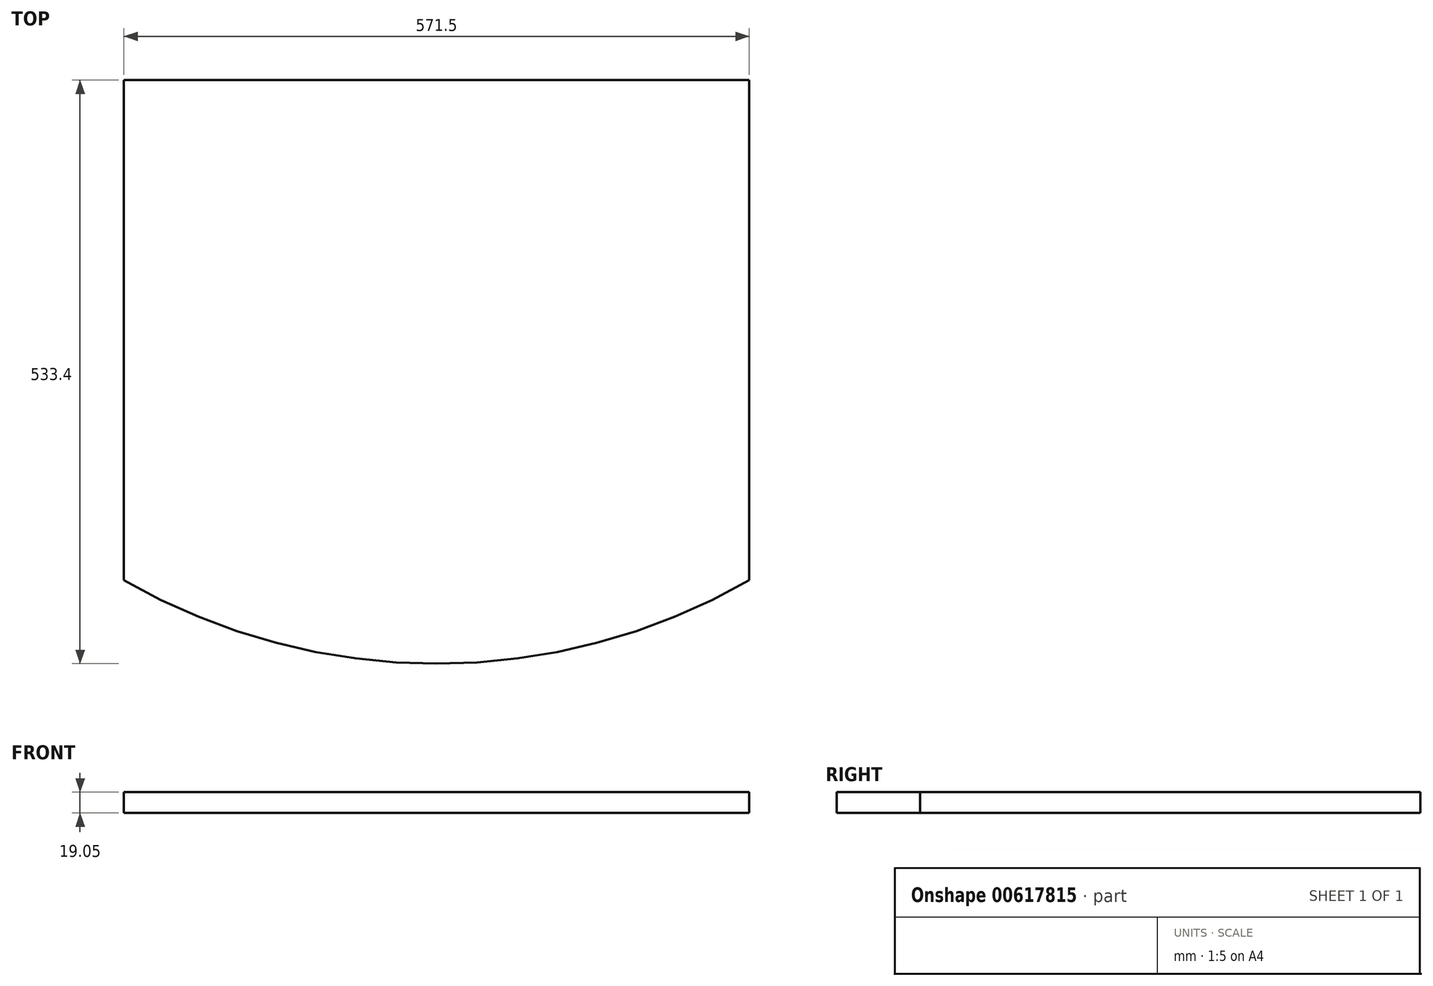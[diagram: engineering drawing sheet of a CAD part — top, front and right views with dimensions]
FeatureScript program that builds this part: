
annotation { "Feature Type Name" : "Feature", "Feature Type Description" : "" }
export const myFeature = defineFeature(function(context is Context, id is Id, definition is map)
    precondition{}
    {
        {
            var Q0;
            Q0=qCreatedBy(makeId("Top.planeOp"),FACE);
            var sketch = newSketch(context, id + "F0", { "sketchPlane" : qUnion([Q0])});
            skLineSegment(sketch, "E0.bottom", {"start": v(-285.75, 228.6) * mm, "end": v(285.75, 228.6) * mm});
            skLineSegment(sketch, "E0.top", {"start": v(-285.75, -228.6) * mm, "end": v(285.75, -228.6) * mm});
            skLineSegment(sketch, "E0.left", {"start": v(-285.75, 228.6) * mm, "end": v(-285.75, -228.6) * mm});
            skLineSegment(sketch, "E0.right", {"start": v(285.75, 228.6) * mm, "end": v(285.75, -228.6) * mm});
            skPoint(sketch, "E0.middle", {"position": v(0, 0) * mm});
            skLineSegment(sketch, "E1", {"start": v(0, -228.6) * mm, "end": v(0, -304.8) * mm});
            skPoint(sketch, "E1.endSnap0", {"position": v(0, -228.6) * mm});
            skArc(sketch, "E2", {"start": v(-285.75, -228.6) * mm, "mid": v(0, -304.8) * mm, "end": v(285.75, -228.6) * mm});
            skSolve(sketch);
        }
        {
            var Q0;
            Q0=makeQuery(id+"F0.imprint","IMPRINT",FACE,{"disambiguationData":[TD([[makeQuery(id+"F0.imprint","IMPRINT",EDGE,{"derivedFrom":sQuery(id+"F0.wireOp",EDGE,"E0.bottom")}),-1.0]])]});
            var Q1;
            {var subQ3=sQuery(id+"F0.wireOp",EDGE,"E1");Q1=makeQuery(id+"F0.imprint","IMPRINT",FACE,{"disambiguationData":[TD([[makeQuery(id+"F0.imprint","IMPRINT",EDGE,{"derivedFrom":subQ3}),-1.0]])]});}
            var Q2;
            {var subQ3=sQuery(id+"F0.wireOp",EDGE,"E1");Q2=makeQuery(id+"F0.imprint","IMPRINT",FACE,{"disambiguationData":[TD([[makeQuery(id+"F0.imprint","IMPRINT",EDGE,{"derivedFrom":subQ3}),1.0]])]});}
            extrude(context, id + "F1", {"entities" : qUnion([Q0, Q1, Q2]), "depth" : 19.05 * mm, "offsetDistance" : 25.4 * mm});
        }
    });
